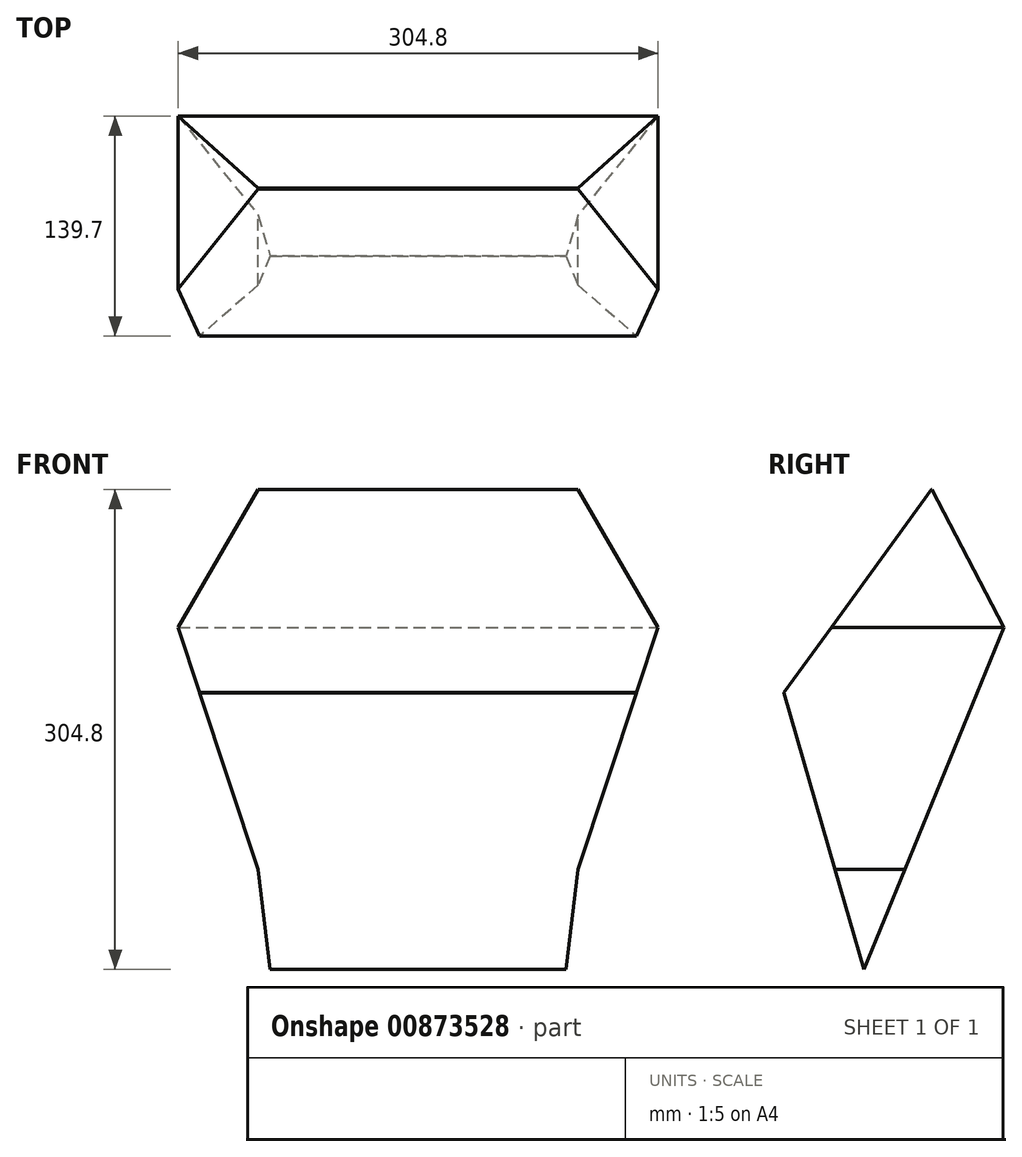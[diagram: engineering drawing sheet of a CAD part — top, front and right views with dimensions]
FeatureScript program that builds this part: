
annotation { "Feature Type Name" : "Feature", "Feature Type Description" : "" }
export const myFeature = defineFeature(function(context is Context, id is Id, definition is map)
    precondition{}
    {
        {
            var Q0;
            Q0=qCreatedBy(makeId("Front.planeOp"),FACE);
            var sketch = newSketch(context, id + "F0", { "sketchPlane" : qUnion([Q0])});
            skLineSegment(sketch, "E0", {"start": v(-152.4, 12.7) * mm, "end": v(-101.6, -140.97) * mm});
            skLineSegment(sketch, "E1", {"start": v(0, -204.47) * mm, "end": v(0, 100.33) * mm});
            skLineSegment(sketch, "E2", {"start": v(-152.4, 12.7) * mm, "end": v(-101.6, 100.33) * mm});
            skLineSegment(sketch, "E3", {"start": v(-101.6, -140.97) * mm, "end": v(-93.98, -204.47) * mm});
            skLineSegment(sketch, "E4", {"start": v(-93.98, -204.47) * mm, "end": v(0, -204.47) * mm});
            skLineSegment(sketch, "E5", {"start": v(-101.6, 100.33) * mm, "end": v(0, 100.33) * mm});
            skLineSegment(sketch, "E6.MirrorCS", {"start": v(101.6, 100.33) * mm, "end": v(0, 100.33) * mm});
            skLineSegment(sketch, "E7.MirrorCS", {"start": v(152.4, 12.7) * mm, "end": v(101.6, 100.33) * mm});
            skLineSegment(sketch, "E8.MirrorCS", {"start": v(152.4, 12.7) * mm, "end": v(101.6, -140.97) * mm});
            skLineSegment(sketch, "E9.MirrorCS", {"start": v(101.6, -140.97) * mm, "end": v(93.98, -204.47) * mm});
            skLineSegment(sketch, "E10.MirrorCS", {"start": v(93.98, -204.47) * mm, "end": v(0, -204.47) * mm});
            skSolve(sketch);
        }
        {
            var Q0;
            Q0=makeQuery(id+"F0.imprint","IMPRINT",FACE,{"disambiguationData":[TD([[makeQuery(id+"F0.imprint","IMPRINT",EDGE,{"derivedFrom":sQuery(id+"F0.wireOp",EDGE,"E0")}),1.0]])]});
            var Q1;
            {var subQ1=sQuery(id+"F0.wireOp",EDGE,"E1");Q1=makeQuery(id+"F0.imprint","IMPRINT",FACE,{"disambiguationData":[TD([[makeQuery(id+"F0.imprint","IMPRINT",EDGE,{"derivedFrom":subQ1}),-1.0]])]});}
            extrude(context, id + "F1", {"entities" : qUnion([Q0, Q1]), "depth" : 139.7 * mm, "offsetDistance" : 25.4 * mm});
        }
        {
            var Q0;
            Q0=qCreatedBy(makeId("Right.planeOp"),FACE);
            var sketch = newSketch(context, id + "F2", { "sketchPlane" : qUnion([Q0])});
            skLineSegment(sketch, "E11", {"start": v(-45.92, 100.63) * mm, "end": v(0, 12.7) * mm});
            skLineSegment(sketch, "E12", {"start": v(0, 12.7) * mm, "end": v(-88.98, -204.56) * mm});
            skLineSegment(sketch, "E13", {"start": v(-88.98, -204.56) * mm, "end": v(-139.71, -28.68) * mm});
            skLineSegment(sketch, "E14", {"start": v(-139.71, -28.68) * mm, "end": v(-46.02, 100.63) * mm});
            skLineSegment(sketch, "E15", {"start": v(-46.02, 100.63) * mm, "end": v(-152.16, 100.63) * mm});
            skLineSegment(sketch, "E16", {"start": v(-152.16, 100.63) * mm, "end": v(-152.16, -218.68) * mm});
            skLineSegment(sketch, "E17", {"start": v(-152.16, -218.68) * mm, "end": v(11.3, -218.68) * mm});
            skLineSegment(sketch, "E18", {"start": v(11.3, -218.68) * mm, "end": v(11.3, 100.63) * mm});
            skLineSegment(sketch, "E19", {"start": v(11.3, 100.63) * mm, "end": v(-45.92, 100.63) * mm});
            skSolve(sketch);
        }
        {
            var Q0;
            Q0 = qSketchRegion(id + "F2", true);
            extrude(context, id + "F3", {"entities" : qUnion([Q0]), "operationType" : NewBodyOperationType.REMOVE, "endBound" : BoundingType.SYMMETRIC, "oppositeDirection" : true, "depth" : 508 * mm, "offsetDistance" : 25.4 * mm});
        }
    });
